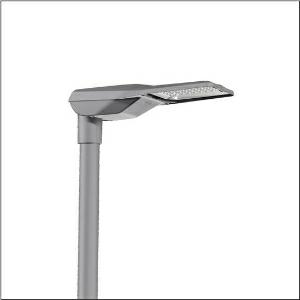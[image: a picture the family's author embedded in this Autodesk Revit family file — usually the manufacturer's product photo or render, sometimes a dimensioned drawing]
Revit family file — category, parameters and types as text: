
# Revit family: streetlight_sl_21_iq_mini___stw1_0a_5xe2e41g08jb_4c9f
name_source: partatom
category: Lighting Fixtures
units: mm (PartAtom-declared; Revit-internal decimal feet)

## family parameters
Cut with Voids When Loaded = No
Host = Face
Light Source = No
Part Type = Normal
Room Calculation Point = No
Round Connector Dimension = Use Diameter
Shared = No

## types (1)
- --- (1 x LED, 11290 lm, 71.6 W, 4000K)
    Apparent Load = 72 VA
    CIE Flux Codes = 39 75 98 100 100
    Color Rendering = 70
    Color Temperature = 4000K
    Default Elevation = 1800 mm
    Description = Streetlight SL 21 iQ mini, mast luminaire, primary light control with lens, of PMMA, primary optical cover: cover, of toughened safety glass, transparent, light distribution: STW1.0a, light emission: direct distribution, primary light characteristic: asymmetric, installation type: post-top, side-entry, LED, High Power LED, rated luminous flux: 11.290lm, luminous efficacy: 158lm/W, light colour: 740, colour temperature: 4000K, control gear: iQ Street-Remote, control: Street-Remote, Auto-Match, Temp-Guard, Lumen-Switch, Night-Set, Smart-Wire, Light-Fading, Desk-Remote (wireless, voltage-free reading and setting of iQ features in the workshop via application-optimized NFC function/RFID function), optimised constant luminous flux control (CLO 2.0), pre-setting: linear dimming characteristic, mains connection: 220..240V, AC, 50/60Hz, start of lifetime: 72W, end of service life: 75W, reduction: 33W, luminaire housing, of diecast aluminium, powder-coated, Siteco® metallic grey (DB 702S), corrosivity category C5 mid according to DIN EN ISO 12944, please order mast flange separately, inclination adjustable: 0°, 5°, 10°, 15°, sealing non-destructively replaceable, multi-level sealing system, length: 628mm, width: 235mm, height: 110mm, mast flange for spigot size: 42mm (side-entry): 5XC10008XM4, 60/48mm (side-entry/post-top): 5XC10108XM2, 76/60mm (side-entry/post-top): 5XC10108XM1, mounting height: 4..8m, protection rating (complete): IP66, insulation class (complete): insulation class II (safety insulation), certification: CE, ENEC, ENEC+, VDE, impact resistance: IK10, permissible operating ambient temperature for outdoor applications: -40..+50°C, standard-compliant lighting for roads and squares, packaging unit: 1 piece

Light Distribution: STW1.0a
    Height = 110 mm
    Lamp = 1 x LED
    Lamp Light Flux = 11290 lm
    Lamp Power = 71.6 W
    Lamp count = 1
    Length = 625 mm
    Luminous efficacy = 158 lm/W
    Manufacturer = Siteco
    ModVariant = No
    Model = 5XE2E41G08JB
    Number of Poles = 1
    OnlyDefault = Yes
    Power Factor = 1
    Product Name = Streetlight SL 21 iQ mini | STW1.0a
    Product group = mast luminaire | pylon top
    ProductGroupID = 6100
    Protection Class = Protection class II
    Protection Degree = IP 66
    RLX_Detail_Level = 1
    RLX_Emergency_Light_Flux = 0 lm
    RLX_Emergency_Type = 0
    RLX_Emergency_Type_DB = No
    RlxData = <blob elided: 26401 chars, md5=65f077de>
    Socket = socket
    Standby Power = 0 W
    System Light Flux = 11290 lm
    System Power = 72 W
    Type Comments = factory setting: luminous flux: 100 % | dim-lin: 254 | 746 mA
    Type Image = l_1003519.jpg
    URL = http://relux.com
    VarID = @adj_170120
    Voltage = 0 V
    Weight = 0.00 kg
    Width = 234 mm

## geometry (parser evidence)
native form markers: Blend x4, Sweep x12
no freeform markers — native parametric forms only
